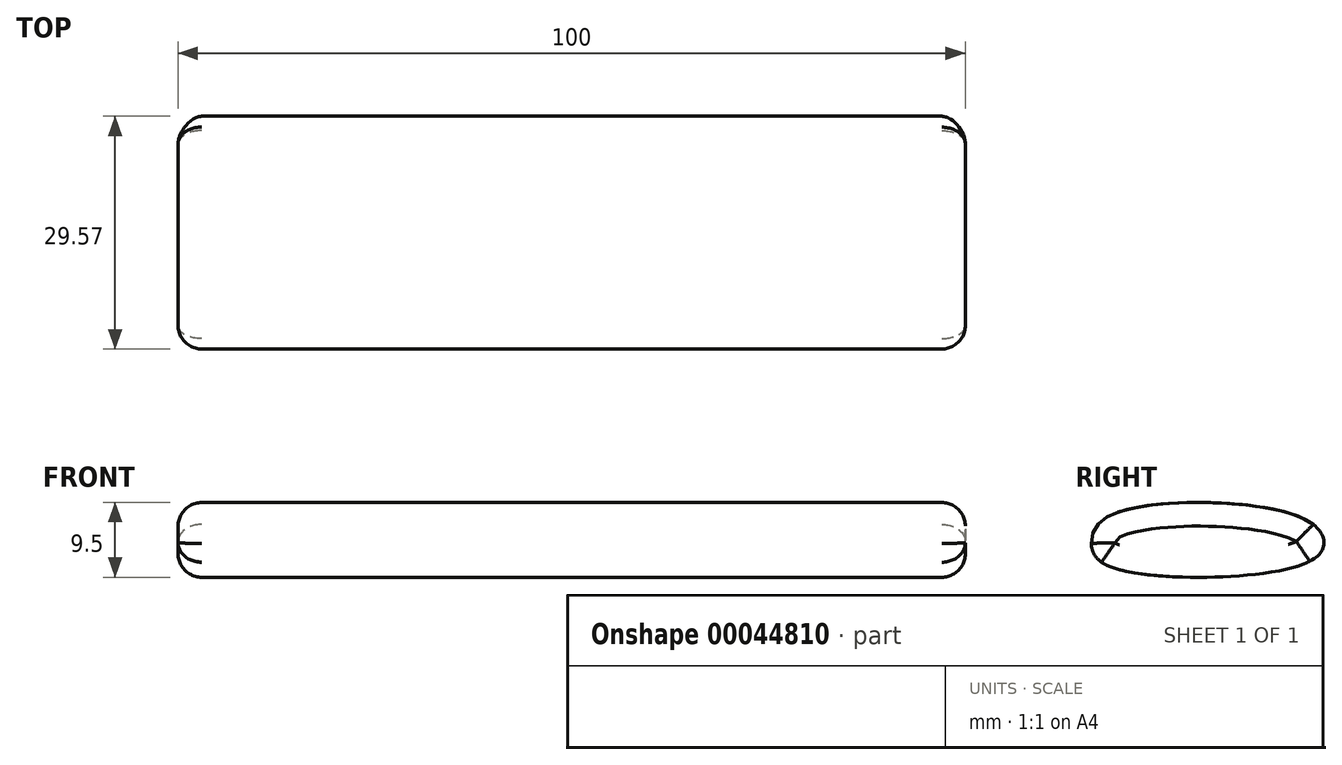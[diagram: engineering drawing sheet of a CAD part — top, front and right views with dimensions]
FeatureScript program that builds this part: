
annotation { "Feature Type Name" : "Feature", "Feature Type Description" : "" }
export const myFeature = defineFeature(function(context is Context, id is Id, definition is map)
    precondition{}
    {
        {
            var Q0;
            Q0=qCreatedBy(makeId("Right.planeOp"),FACE);
            var sketch = newSketch(context, id + "F0", { "sketchPlane" : qUnion([Q0])});
            skFitSpline(sketch, "E0", {"points": [v(16.89, 5) * mm, v(14.42, 8) * mm, v(16.89, 11.6) * mm, v(40.31, 11.6) * mm, v(43.98, 8) * mm, v(40.31, 5) * mm, v(16.89, 5) * mm]});
            skLineSegment(sketch, "E1", {"start": v(16.89, 5) * mm, "end": v(40.31, 5) * mm});
            skSolve(sketch);
        }
        {
            var Q0;
            Q0=makeQuery(id+"F0.imprint","IMPRINT",FACE,{"disambiguationData":[TD([[makeQuery(id+"F0.imprint","IMPRINT",EDGE,{"derivedFrom":sQuery(id+"F0.wireOp",EDGE,"E0")}),-1.0]])]});
            extrude(context, id + "F1", {"entities" : qUnion([Q0]), "depth" : 50 * mm, "hasSecondDirection" : true, "secondDirectionOppositeDirection" : true, "secondDirectionDepth" : 50 * mm});
        }
        {
            var Q0;
            Q0=makeQuery(id+"F1.opExtrude","CAP_EDGE",EDGE,{"disambiguationData":[OSD([sQuery(id+"F0.wireOp",EDGE,"E0")])],"isStart":false});
            var Q1;
            Q1=makeQuery(id+"F1.opExtrude","CAP_EDGE",EDGE,{"disambiguationData":[OSD([sQuery(id+"F0.wireOp",EDGE,"E0")])],"isStart":true});
            fillet(context, id + "F2", {"entities" : qUnion([Q0, Q1]), "radius" : 3 * mm, "tangentPropagation" : true, "allowEdgeOverflow" : false});
        }
    });
